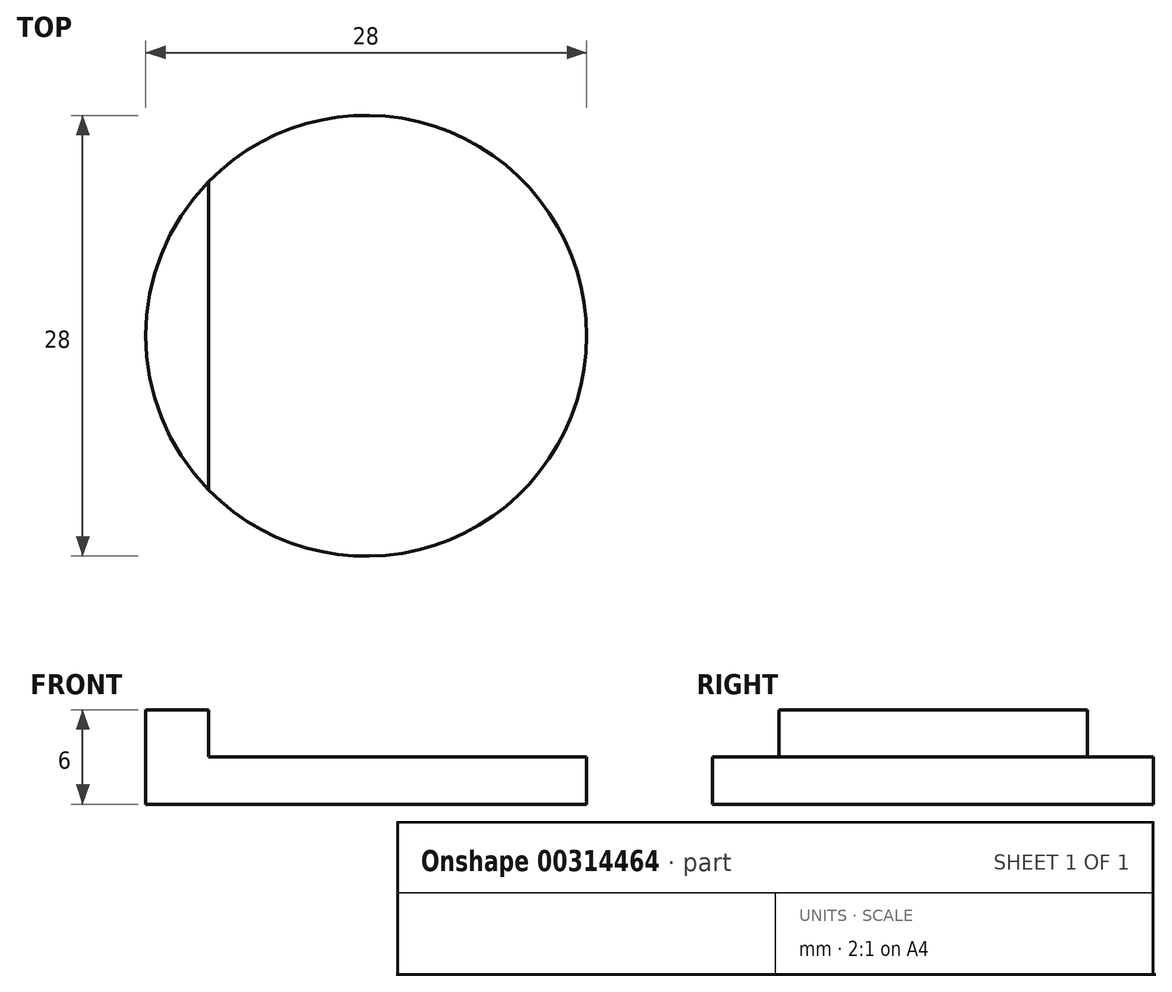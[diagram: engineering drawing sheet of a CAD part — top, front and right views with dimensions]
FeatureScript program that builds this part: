
annotation { "Feature Type Name" : "Feature", "Feature Type Description" : "" }
export const myFeature = defineFeature(function(context is Context, id is Id, definition is map)
    precondition{}
    {
        {
            var Q0;
            Q0=qCreatedBy(makeId("Top.planeOp"),FACE);
            var sketch = newSketch(context, id + "F0", { "sketchPlane" : qUnion([Q0])});
            skCircle(sketch, "E0", {"center": v(0, 0) * mm, "radius": 14 * mm});
            skSolve(sketch);
        }
        {
            var Q0;
            Q0=makeQuery(id+"F0.imprint","IMPRINT",FACE,{"disambiguationData":[TD([[makeQuery(id+"F0.imprint","IMPRINT",EDGE,{"derivedFrom":sQuery(id+"F0.wireOp",EDGE,"E0")}),1.0]])]});
            extrude(context, id + "F1", {"entities" : qUnion([Q0]), "depth" : 3 * mm});
        }
        {
            var Q0;
            Q0=makeQuery(id+"F1.opExtrude","CAP_FACE",FACE,{"disambiguationData":[OSD([sQuery(id+"F0.wireOp",EDGE,"E0")])],"isStart":false});
            var sketch = newSketch(context, id + "F2", { "sketchPlane" : qUnion([Q0])});
            skLineSegment(sketch, "E1.bottom", {"start": v(-10, -14) * mm, "end": v(-14, -14) * mm});
            skLineSegment(sketch, "E1.top", {"start": v(-10, 14) * mm, "end": v(-14, 14) * mm});
            skLineSegment(sketch, "E1.left", {"start": v(-10, -14) * mm, "end": v(-10, 14) * mm});
            skLineSegment(sketch, "E1.right", {"start": v(-14, -14) * mm, "end": v(-14, 14) * mm});
            skPoint(sketch, "E1.middle", {"position": v(-12, 0) * mm});
            skLineSegment(sketch, "E2.1.0.0", {"start": v(-6, -14) * mm, "end": v(-10, -14) * mm});
            skLineSegment(sketch, "E2.1.0.1", {"start": v(-6, 14) * mm, "end": v(-10, 14) * mm});
            skLineSegment(sketch, "E2.1.0.2", {"start": v(-6, -14) * mm, "end": v(-6, 14) * mm});
            skPoint(sketch, "E2.1.0.4", {"position": v(-8, 0) * mm});
            skLineSegment(sketch, "E2.2.0.0", {"start": v(-2, -14) * mm, "end": v(-6, -14) * mm});
            skLineSegment(sketch, "E2.2.0.1", {"start": v(-2, 14) * mm, "end": v(-6, 14) * mm});
            skLineSegment(sketch, "E2.2.0.2", {"start": v(-2, -14) * mm, "end": v(-2, 14) * mm});
            skLineSegment(sketch, "E2.2.0.3", {"start": v(-6, -14) * mm, "end": v(-6, 14) * mm});
            skPoint(sketch, "E2.2.0.4", {"position": v(-4, 0) * mm});
            skLineSegment(sketch, "E2.direction1", {"start": v(-14, -14) * mm, "end": v(-10, -14) * mm, "construction": true});
            skLineSegment(sketch, "E3.0.3.0", {"start": v(2, -14) * mm, "end": v(-2, -14) * mm});
            skLineSegment(sketch, "E3.3.3.0", {"start": v(2, 14) * mm, "end": v(-2, 14) * mm});
            skLineSegment(sketch, "E3.6.3.0", {"start": v(2, -14) * mm, "end": v(2, 14) * mm});
            skPoint(sketch, "E3.12.3.0", {"position": v(0, 0) * mm});
            skLineSegment(sketch, "E3.0.4.0", {"start": v(6, -14) * mm, "end": v(2, -14) * mm});
            skLineSegment(sketch, "E3.3.4.0", {"start": v(6, 14) * mm, "end": v(2, 14) * mm});
            skLineSegment(sketch, "E3.6.4.0", {"start": v(6, -14) * mm, "end": v(6, 14) * mm});
            skLineSegment(sketch, "E3.9.4.0", {"start": v(2, -14) * mm, "end": v(2, 14) * mm});
            skPoint(sketch, "E3.12.4.0", {"position": v(4, 0) * mm});
            skLineSegment(sketch, "E3.0.5.0", {"start": v(10, -14) * mm, "end": v(6, -14) * mm});
            skLineSegment(sketch, "E3.3.5.0", {"start": v(10, 14) * mm, "end": v(6, 14) * mm});
            skLineSegment(sketch, "E3.6.5.0", {"start": v(10, -14) * mm, "end": v(10, 14) * mm});
            skLineSegment(sketch, "E3.9.5.0", {"start": v(6, -14) * mm, "end": v(6, 14) * mm});
            skPoint(sketch, "E3.12.5.0", {"position": v(8, 0) * mm});
            skLineSegment(sketch, "E3.0.6.0", {"start": v(14, -14) * mm, "end": v(10, -14) * mm});
            skLineSegment(sketch, "E3.3.6.0", {"start": v(14, 14) * mm, "end": v(10, 14) * mm});
            skLineSegment(sketch, "E3.6.6.0", {"start": v(14, -14) * mm, "end": v(14, 14) * mm});
            skLineSegment(sketch, "E3.9.6.0", {"start": v(10, -14) * mm, "end": v(10, 14) * mm});
            skPoint(sketch, "E3.12.6.0", {"position": v(12, 0) * mm});
            skLineSegment(sketch, "E3.0.7.0", {"start": v(18, -14) * mm, "end": v(14, -14) * mm});
            skLineSegment(sketch, "E3.3.7.0", {"start": v(18, 14) * mm, "end": v(14, 14) * mm});
            skLineSegment(sketch, "E3.6.7.0", {"start": v(18, -14) * mm, "end": v(18, 14) * mm});
            skLineSegment(sketch, "E3.9.7.0", {"start": v(14, -14) * mm, "end": v(14, 14) * mm});
            skPoint(sketch, "E3.12.7.0", {"position": v(16, 0) * mm});
            skSolve(sketch);
        }
        {
            var Q0;
            {var subQ0=sQuery(id+"F2.wireOp",EDGE,"E3.9.4.0");var subQ1=makeQuery(id+"F1.opExtrude","CAP_EDGE",EDGE,{"disambiguationData":[OSD([sQuery(id+"F0.wireOp",EDGE,"E0")])],"isStart":false});var subQ2=makeQuery(id+"F2.imprint","INTERSECT",VERTEX,{"disambiguationData":[OD(0.0)],"derivedFrom":[subQ1,subQ0]});Q0=makeQuery(id+"F2.imprint","IMPRINT",FACE,{"disambiguationData":[TD([[makeQuery(id+"F2.imprint","IMPRINT",EDGE,{"disambiguationData":[TD([[subQ2,-1.0]])],"derivedFrom":subQ0}),-1.0]])]});}
            var Q1;
            {var subQ0=sQuery(id+"F2.wireOp",EDGE,"E1.left");var subQ1=makeQuery(id+"F1.opExtrude","CAP_EDGE",EDGE,{"disambiguationData":[OSD([sQuery(id+"F0.wireOp",EDGE,"E0")])],"isStart":false});var subQ2=makeQuery(id+"F2.imprint","INTERSECT",VERTEX,{"disambiguationData":[OD(0.0)],"derivedFrom":[subQ1,subQ0]});Q1=makeQuery(id+"F2.imprint","IMPRINT",FACE,{"disambiguationData":[TD([[makeQuery(id+"F2.imprint","IMPRINT",EDGE,{"disambiguationData":[TD([[subQ2,-1.0]])],"derivedFrom":subQ0}),1.0]])]});}
            var Q2;
            {var subQ0=sQuery(id+"F2.wireOp",EDGE,"E2.2.0.3");var subQ1=makeQuery(id+"F1.opExtrude","CAP_EDGE",EDGE,{"disambiguationData":[OSD([sQuery(id+"F0.wireOp",EDGE,"E0")])],"isStart":false});var subQ2=makeQuery(id+"F2.imprint","INTERSECT",VERTEX,{"disambiguationData":[OD(0.0)],"derivedFrom":[subQ1,subQ0]});Q2=makeQuery(id+"F2.imprint","IMPRINT",FACE,{"disambiguationData":[TD([[makeQuery(id+"F2.imprint","IMPRINT",EDGE,{"disambiguationData":[TD([[subQ2,-1.0]])],"derivedFrom":subQ0}),-1.0]])]});}
            var Q3;
            {var subQ0=sQuery(id+"F2.wireOp",EDGE,"E3.9.6.0");var subQ1=makeQuery(id+"F1.opExtrude","CAP_EDGE",EDGE,{"disambiguationData":[OSD([sQuery(id+"F0.wireOp",EDGE,"E0")])],"isStart":false});var subQ2=makeQuery(id+"F2.imprint","INTERSECT",VERTEX,{"disambiguationData":[OD(0.0)],"derivedFrom":[subQ1,subQ0]});Q3=makeQuery(id+"F2.imprint","IMPRINT",FACE,{"disambiguationData":[TD([[makeQuery(id+"F2.imprint","IMPRINT",EDGE,{"disambiguationData":[TD([[subQ2,-1.0]])],"derivedFrom":subQ0}),-1.0]])]});}
            extrude(context, id + "F3", {"entities" : qUnion([Q0, Q1, Q2, Q3]), "operationType" : NewBodyOperationType.ADD, "depth" : 3 * mm});
        }
    });
